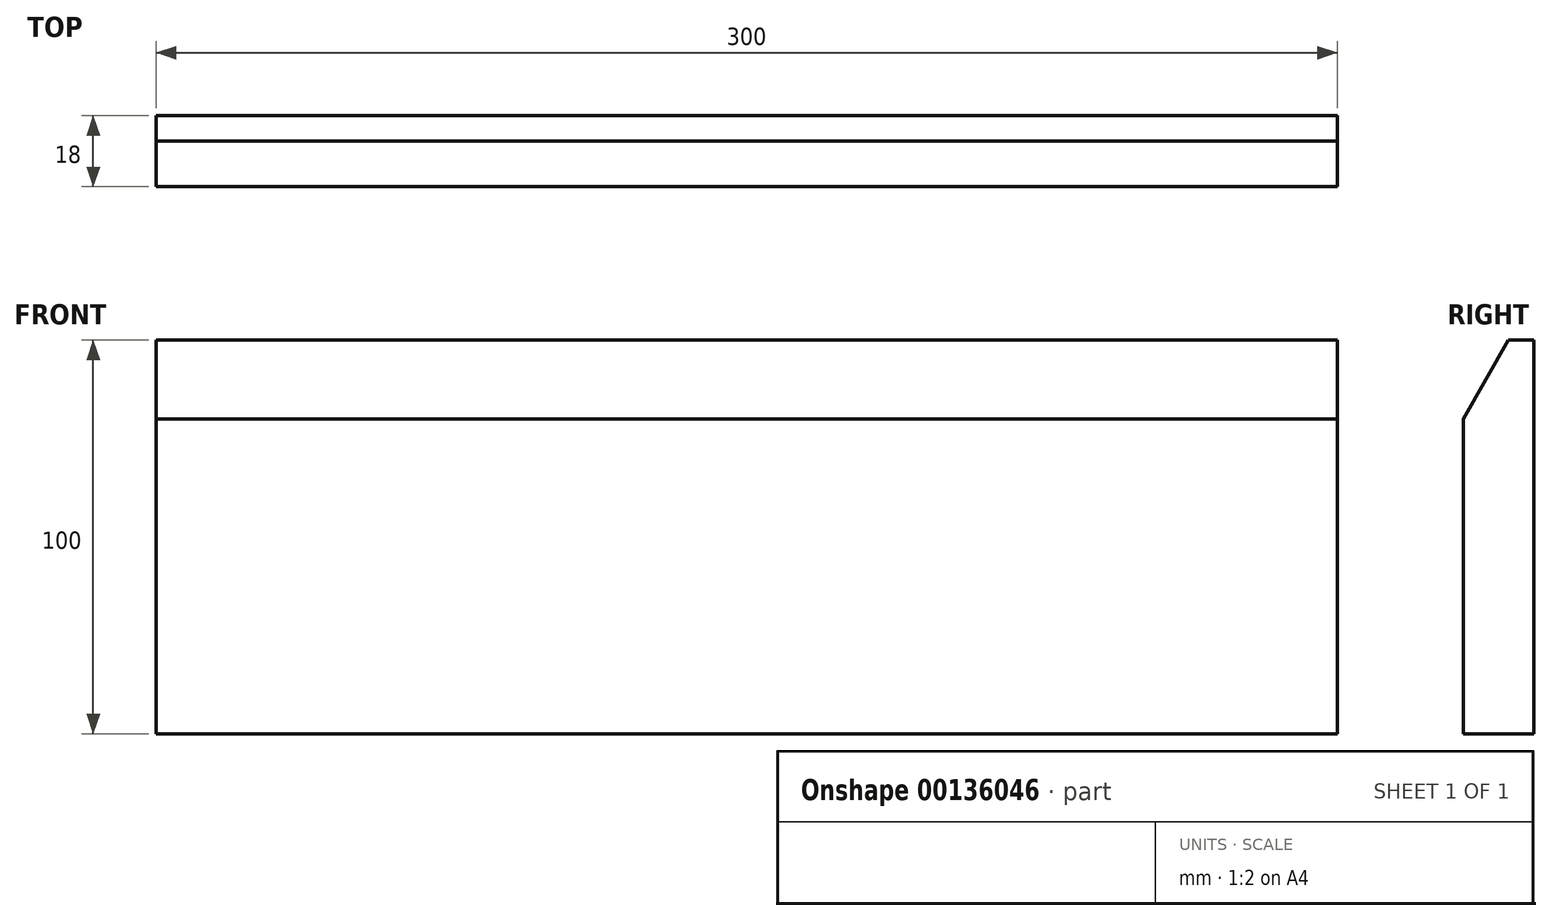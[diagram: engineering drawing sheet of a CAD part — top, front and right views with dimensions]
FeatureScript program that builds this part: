
annotation { "Feature Type Name" : "Feature", "Feature Type Description" : "" }
export const myFeature = defineFeature(function(context is Context, id is Id, definition is map)
    precondition{}
    {
        {
            var Q0;
            Q0=qCreatedBy(makeId("Front.planeOp"),FACE);
            var sketch = newSketch(context, id + "F0", { "sketchPlane" : qUnion([Q0])});
            skLineSegment(sketch, "E0.bottom", {"start": v(-153.72, -55.78) * mm, "end": v(146.28, -55.78) * mm});
            skLineSegment(sketch, "E0.top", {"start": v(-153.72, -155.78) * mm, "end": v(146.28, -155.78) * mm});
            skLineSegment(sketch, "E0.left", {"start": v(-153.72, -55.78) * mm, "end": v(-153.72, -155.78) * mm});
            skLineSegment(sketch, "E0.right", {"start": v(146.28, -55.78) * mm, "end": v(146.28, -155.78) * mm});
            skSolve(sketch);
        }
        {
            var Q0;
            Q0=makeQuery(id+"F0.imprint","IMPRINT",FACE,{"disambiguationData":[TD([[makeQuery(id+"F0.imprint","IMPRINT",EDGE,{"derivedFrom":sQuery(id+"F0.wireOp",EDGE,"E0.bottom")}),-1.0]])]});
            extrude(context, id + "F1", {"entities" : qUnion([Q0]), "endBound" : BoundingType.SYMMETRIC, "depth" : 18 * mm});
        }
        {
            var Q0;
            Q0=makeQuery(id+"F1.opExtrude","SWEPT_FACE",FACE,{"disambiguationData":[OSD([sQuery(id+"F0.wireOp",EDGE,"E0.right")])]});
            var sketch = newSketch(context, id + "F2", { "sketchPlane" : qUnion([Q0])});
            skLineSegment(sketch, "E1", {"start": v(-9, -75.78) * mm, "end": v(-9, -75.78) * mm});
            skLineSegment(sketch, "E2", {"start": v(-9, -75.78) * mm, "end": v(-9, -55.78) * mm});
            skLineSegment(sketch, "E3", {"start": v(-9, -55.78) * mm, "end": v(2.55, -55.78) * mm});
            skLineSegment(sketch, "E4", {"start": v(-9, -75.78) * mm, "end": v(2.55, -55.78) * mm});
            skSolve(sketch);
        }
        {
            var Q0;
            Q0=makeQuery(id+"F2.imprint","IMPRINT",FACE,{"disambiguationData":[TD([[makeQuery(id+"F2.imprint","IMPRINT",EDGE,{"derivedFrom":sQuery(id+"F2.wireOp",EDGE,"E2")}),1.0]])]});
            extrude(context, id + "F3", {"entities" : qUnion([Q0]), "operationType" : NewBodyOperationType.REMOVE, "endBound" : BoundingType.THROUGH_ALL, "oppositeDirection" : true, "depth" : 25 * mm});
        }
    });
